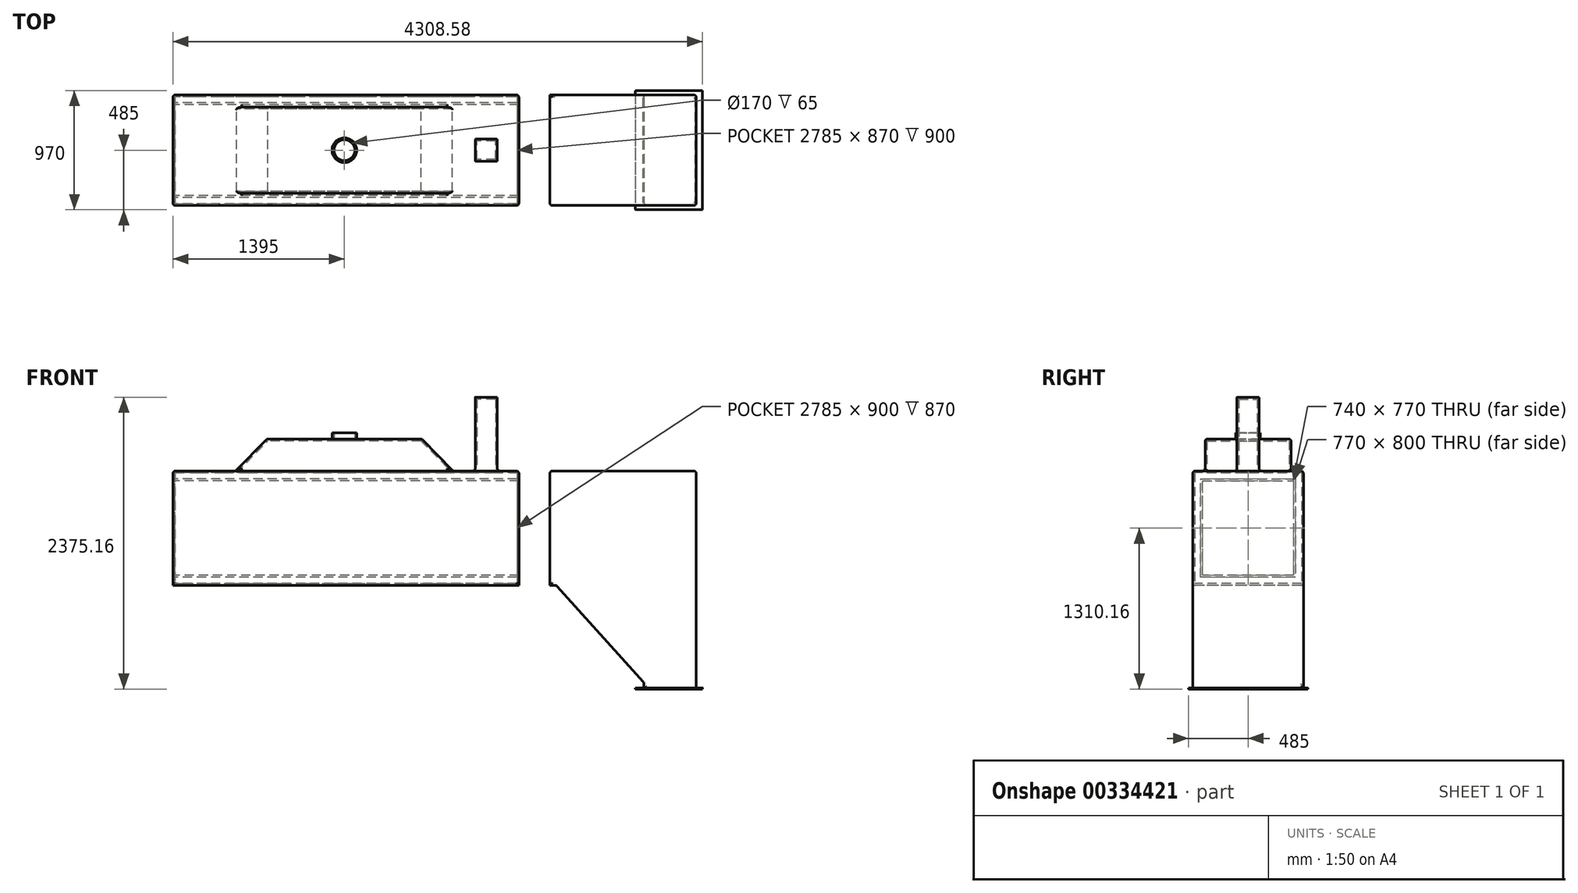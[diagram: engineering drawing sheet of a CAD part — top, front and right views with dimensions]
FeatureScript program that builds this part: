
annotation { "Feature Type Name" : "Feature", "Feature Type Description" : "" }
export const myFeature = defineFeature(function(context is Context, id is Id, definition is map)
    precondition{}
    {
        {
            var Q0;
            Q0=qCreatedBy(makeId("Front.planeOp"),FACE);
            var sketch = newSketch(context, id + "F0", { "sketchPlane" : qUnion([Q0])});
            skLineSegment(sketch, "E0.bottom", {"start": v(1420, 465) * mm, "end": v(-1420, 465) * mm});
            skLineSegment(sketch, "E0.top", {"start": v(1420, -465) * mm, "end": v(-1420, -465) * mm});
            skLineSegment(sketch, "E0.left", {"start": v(1420, 465) * mm, "end": v(1420, -465) * mm});
            skLineSegment(sketch, "E0.right", {"start": v(-1420, 465) * mm, "end": v(-1420, -465) * mm});
            skPoint(sketch, "E0.middle", {"position": v(0, 0) * mm});
            skSolve(sketch);
        }
        {
            var Q0;
            Q0 = qSketchRegion(id + "F0", true);
            extrude(context, id + "F1", {"entities" : qUnion([Q0]), "oppositeDirection" : true, "depth" : 900 * mm});
        }
        {
            var Q0;
            Q0=makeQuery(id+"F1.opExtrude","SWEPT_FACE",FACE,{"disambiguationData":[OSD([sQuery(id+"F0.wireOp",EDGE,"E0.bottom")])]});
            var sketch = newSketch(context, id + "F2", { "sketchPlane" : qUnion([Q0])});
            skLineSegment(sketch, "E1.bottom", {"start": v(885, 100) * mm, "end": v(-885, 100) * mm});
            skLineSegment(sketch, "E1.top", {"start": v(885, 800) * mm, "end": v(-885, 800) * mm});
            skLineSegment(sketch, "E1.left", {"start": v(885, 100) * mm, "end": v(885, 800) * mm});
            skLineSegment(sketch, "E1.right", {"start": v(-885, 100) * mm, "end": v(-885, 800) * mm});
            skPoint(sketch, "E1.middle", {"position": v(0, 450) * mm});
            skLineSegment(sketch, "E2", {"start": v(26.19, 450) * mm, "end": v(-1737.19, 450) * mm, "construction": true});
            skSolve(sketch);
        }
        {
            var Q0;
            Q0=makeQuery(id+"F2.imprint","IMPRINT",FACE,{"disambiguationData":[TD([[makeQuery(id+"F2.imprint","IMPRINT",EDGE,{"derivedFrom":sQuery(id+"F2.wireOp",EDGE,"E1.bottom")}),1.0]])]});
            cPlane(context, id + "F3", {"entities" : qUnion([Q0]), "cplaneType" : CPlaneType.OFFSET, "offset" : 260 * mm, "width" : 150 * mm, "height" : 150 * mm});
        }
        {
            var Q0;
            Q0=qCreatedBy(id+"F3.planeOp",FACE);
            var sketch = newSketch(context, id + "F4", { "sketchPlane" : qUnion([Q0])});
            skLineSegment(sketch, "E3.0", {"start": v(630, 800) * mm, "end": v(-630, 800) * mm});
            skLineSegment(sketch, "E3.1", {"start": v(630, 100) * mm, "end": v(-630, 100) * mm});
            skLineSegment(sketch, "E4", {"start": v(0, 800) * mm, "end": v(0, 100) * mm, "construction": true});
            skLineSegment(sketch, "E5", {"start": v(-630, 800) * mm, "end": v(-630, 100) * mm});
            skLineSegment(sketch, "E6.MirrorCS", {"start": v(630, 800) * mm, "end": v(630, 100) * mm});
            skPoint(sketch, "E7.orphan", {"position": v(-885, 800) * mm});
            skPoint(sketch, "E8.orphan", {"position": v(-885, 100) * mm});
            skPoint(sketch, "E9.orphan", {"position": v(885, 100) * mm});
            skPoint(sketch, "E10.orphan", {"position": v(885, 800) * mm});
            skSolve(sketch);
        }
        {
            var Q1;
            Q1=makeQuery(id+"F2.imprint","IMPRINT",FACE,{"disambiguationData":[TD([[makeQuery(id+"F2.imprint","IMPRINT",EDGE,{"derivedFrom":sQuery(id+"F2.wireOp",EDGE,"E1.bottom")}),-1.0]])]});
            var Q2;
            Q2=makeQuery(id+"F4.imprint","IMPRINT",FACE,{"disambiguationData":[TD([[makeQuery(id+"F4.imprint","IMPRINT",EDGE,{"derivedFrom":sQuery(id+"F4.wireOp",EDGE,"E3.0")}),1.0]])]});
            loft(context, id + "F5", {"operationType" : NewBodyOperationType.ADD, "sheetProfilesArray" : [{ "sheetProfileEntities" : qUnion([Q1]) }, { "sheetProfileEntities" : qUnion([Q2]) }]});
        }
        {
            var Q0;
            Q0=makeQuery(id+"F4.imprint","IMPRINT",FACE,{"disambiguationData":[TD([[makeQuery(id+"F4.imprint","IMPRINT",EDGE,{"derivedFrom":sQuery(id+"F4.wireOp",EDGE,"E3.0")}),1.0]])]});
            var sketch = newSketch(context, id + "F6", { "sketchPlane" : qUnion([Q0])});
            skCircle(sketch, "E11", {"center": v(0, 450) * mm, "radius": 100 * mm});
            skSolve(sketch);
        }
        {
            var Q0;
            Q0 = qSketchRegion(id + "F6", true);
            extrude(context, id + "F7", {"entities" : qUnion([Q0]), "operationType" : NewBodyOperationType.ADD, "depth" : 50 * mm});
        }
        {
            var Q0;
            Q0=makeQuery(id+"F1.opExtrude","SWEPT_FACE",FACE,{"disambiguationData":[OSD([sQuery(id+"F0.wireOp",EDGE,"E0.bottom")])]});
            var sketch = newSketch(context, id + "F8", { "sketchPlane" : qUnion([Q0])});
            skLineSegment(sketch, "E12.bottom", {"start": v(1239.32, 360) * mm, "end": v(1069.32, 360) * mm});
            skLineSegment(sketch, "E12.top", {"start": v(1239.32, 540) * mm, "end": v(1069.32, 540) * mm});
            skLineSegment(sketch, "E12.left", {"start": v(1244.32, 365) * mm, "end": v(1244.32, 535) * mm});
            skLineSegment(sketch, "E12.right", {"start": v(1064.32, 365) * mm, "end": v(1064.32, 535) * mm});
            skPoint(sketch, "E12.middle", {"position": v(1154.32, 450) * mm});
            skPoint(sketch, "E13", {"position": v(885, 450) * mm});
            skPoint(sketch, "E14.visualSharp", {"position": v(1064.32, 360) * mm});
            skArc(sketch, "E14.filletArc", {"start": v(1064.32, 365) * mm, "mid": v(1065.79, 361.46) * mm, "end": v(1069.32, 360) * mm});
            skPoint(sketch, "E15.visualSharp", {"position": v(1244.32, 360) * mm});
            skArc(sketch, "E15.filletArc", {"start": v(1239.32, 360) * mm, "mid": v(1242.86, 361.46) * mm, "end": v(1244.32, 365) * mm});
            skPoint(sketch, "E16.visualSharp", {"position": v(1244.32, 540) * mm});
            skArc(sketch, "E16.filletArc", {"start": v(1244.32, 535) * mm, "mid": v(1242.86, 538.54) * mm, "end": v(1239.32, 540) * mm});
            skPoint(sketch, "E17.visualSharp", {"position": v(1064.32, 540) * mm});
            skArc(sketch, "E17.filletArc", {"start": v(1069.32, 540) * mm, "mid": v(1065.79, 538.54) * mm, "end": v(1064.32, 535) * mm});
            skSolve(sketch);
        }
        {
            var Q0;
            Q0 = qSketchRegion(id + "F8", true);
            extrude(context, id + "F9", {"entities" : qUnion([Q0]), "operationType" : NewBodyOperationType.ADD, "depth" : 600 * mm});
        }
        {
            var Q0;
            Q0=makeQuery(id+"F1.opExtrude","SWEPT_FACE",FACE,{"disambiguationData":[OSD([sQuery(id+"F0.wireOp",EDGE,"E0.right")])]});
            extrude(context, id + "F10", {"entities" : qUnion([Q0]), "operationType" : NewBodyOperationType.REMOVE, "oppositeDirection" : true, "depth" : 25 * mm});
        }
        {
            var Q0;
            Q0=makeQuery(id+"F10.boolean.opBoolean","COPY",FACE,{"derivedFrom":makeQuery(id+"F10.opExtrude","CAP_FACE",FACE,{"disambiguationData":[OSD([sQuery(id+"F0.wireOp",EDGE,"E0.right")])],"isStart":false})});
            var sketch = newSketch(context, id + "F11", { "sketchPlane" : qUnion([Q0])});
            skLineSegment(sketch, "E18.0", {"start": v(-820, 385) * mm, "end": v(-820, -385) * mm});
            skLineSegment(sketch, "E18.1", {"start": v(-30, 385) * mm, "end": v(-820, 385) * mm});
            skLineSegment(sketch, "E19.0", {"start": v(-80, -385) * mm, "end": v(-80, 435) * mm});
            skLineSegment(sketch, "E20.0", {"start": v(-820, -385) * mm, "end": v(-80, -385) * mm});
            skSolve(sketch);
        }
        {
            var Q0;
            Q0 = qSketchRegion(id + "F11", true);
            extrude(context, id + "F12", {"entities" : qUnion([Q0]), "operationType" : NewBodyOperationType.REMOVE, "endBound" : BoundingType.THROUGH_ALL, "oppositeDirection" : true, "depth" : 25 * mm});
        }
        {
            var Q0;
            Q0=makeQuery(id+"F7.opExtrude","CAP_FACE",FACE,{"disambiguationData":[OSD([sQuery(id+"F6.wireOp",EDGE,"E11")])],"isStart":false});
            shell(context, id + "F13", {"entities" : qUnion([Q0]), "thickness" : 15 * mm});
        }
        {
            var Q0;
            Q0=qCreatedBy(makeId("Front.planeOp"),FACE);
            var sketch = newSketch(context, id + "F14", { "sketchPlane" : qUnion([Q0])});
            skLineSegment(sketch, "E21", {"start": v(1672.61, 465) * mm, "end": v(2863.58, 465) * mm});
            skLineSegment(sketch, "E22", {"start": v(2863.58, 465) * mm, "end": v(2863.58, -1310.16) * mm});
            skLineSegment(sketch, "E23", {"start": v(2863.58, -1310.16) * mm, "end": v(2438.58, -1310.16) * mm});
            skLineSegment(sketch, "E24", {"start": v(2438.58, -1310.16) * mm, "end": v(2438.58, -1260.16) * mm});
            skLineSegment(sketch, "E25", {"start": v(2438.58, -1260.16) * mm, "end": v(1722.61, -465) * mm});
            skLineSegment(sketch, "E26", {"start": v(1722.61, -465) * mm, "end": v(1672.61, -465) * mm});
            skLineSegment(sketch, "E27", {"start": v(1672.61, -465) * mm, "end": v(1672.61, 465) * mm});
            skSolve(sketch);
        }
        {
            var Q0;
            Q0 = qSketchRegion(id + "F14", true);
            var Q1;
            Q1=makeQuery(id+"F1.opExtrude","CAP_FACE",FACE,{"disambiguationData":[OSD([sQuery(id+"F0.wireOp",EDGE,"E0.bottom"),sQuery(id+"F0.wireOp",EDGE,"E0.top"),sQuery(id+"F0.wireOp",EDGE,"E0.left"),sQuery(id+"F0.wireOp",EDGE,"E0.right")])],"isStart":false});
            extrude(context, id + "F15", {"entities" : qUnion([Q0]), "endBound" : BoundingType.UP_TO_SURFACE, "oppositeDirection" : true, "endBoundEntityFace" : qUnion([Q1]), "offsetDistance" : 25 * mm, "depth" : 25 * mm});
        }
        {
            var Q0;
            Q0=makeQuery(id+"F15.boolean.opBoolean","MERGE",FACE,{"derivedFrom":[makeQuery(id+"F1.opExtrude","SWEPT_FACE",FACE,{"disambiguationData":[OSD([sQuery(id+"F0.wireOp",EDGE,"E0.bottom")])]}),makeQuery(id+"F15.opExtrude","SWEPT_FACE",FACE,{"disambiguationData":[OSD([sQuery(id+"F14.wireOp",EDGE,"E21")])]})]});
            var Q1;
            Q1=makeQuery(id+"F15.boolean.opBoolean","MERGE",FACE,{"derivedFrom":[makeQuery(id+"F1.opExtrude","CAP_FACE",FACE,{"disambiguationData":[OSD([sQuery(id+"F0.wireOp",EDGE,"E0.bottom"),sQuery(id+"F0.wireOp",EDGE,"E0.top"),sQuery(id+"F0.wireOp",EDGE,"E0.left"),sQuery(id+"F0.wireOp",EDGE,"E0.right")])],"isStart":true}),makeQuery(id+"F15.opExtrude","CAP_FACE",FACE,{"disambiguationData":[OSD([sQuery(id+"F14.wireOp",EDGE,"E21"),sQuery(id+"F14.wireOp",EDGE,"E22"),sQuery(id+"F14.wireOp",EDGE,"E23"),sQuery(id+"F14.wireOp",EDGE,"E24"),sQuery(id+"F14.wireOp",EDGE,"E25"),sQuery(id+"F14.wireOp",EDGE,"E26"),sQuery(id+"F14.wireOp",EDGE,"E27")])],"isStart":true})]});
            var Q2;
            Q2=makeQuery(id+"F15.opExtrude","SWEPT_FACE",FACE,{"disambiguationData":[OSD([sQuery(id+"F14.wireOp",EDGE,"E22")])]});
            var Q3;
            {var subQ0=sQuery(id+"F0.wireOp",EDGE,"E0.right");var subQ1=sQuery(id+"F0.wireOp",EDGE,"E0.left");var subQ2=sQuery(id+"F0.wireOp",EDGE,"E0.top");var subQ3=sQuery(id+"F0.wireOp",EDGE,"E0.bottom");Q3=makeQuery(id+"F15.boolean.opBoolean","MERGE",FACE,{"derivedFrom":[makeQuery(id+"F1.opExtrude","CAP_FACE",FACE,{"disambiguationData":[OSD([subQ3,subQ2,subQ1,subQ0])],"isStart":false}),makeQuery(id+"F15.opExtrude","CAP_FACE",FACE,{"disambiguationData":[OSD([subQ3,subQ2,subQ1,subQ0])],"isStart":false})]});}
            var Q4;
            Q4=makeQuery(id+"F15.opExtrude","SWEPT_FACE",FACE,{"disambiguationData":[OSD([sQuery(id+"F14.wireOp",EDGE,"E25")])]});
            var Q5;
            Q5=makeQuery(id+"F5.opLoft","SWEPT_FACE",FACE,{"disambiguationData":[OSD([sQuery(id+"F2.wireOp",EDGE,"E1.top"),sQuery(id+"F2.wireOp",EDGE,"E1.left"),sQuery(id+"F2.wireOp",EDGE,"E1.right"),sQuery(id+"F4.wireOp",EDGE,"E3.0"),sQuery(id+"F4.wireOp",EDGE,"E5"),sQuery(id+"F4.wireOp",EDGE,"E6.MirrorCS")])]});
            var Q6;
            Q6=makeQuery(id+"F5.opLoft","SWEPT_FACE",FACE,{"disambiguationData":[OSD([sQuery(id+"F2.wireOp",EDGE,"E1.bottom"),sQuery(id+"F2.wireOp",EDGE,"E1.top"),sQuery(id+"F2.wireOp",EDGE,"E1.left"),sQuery(id+"F4.wireOp",EDGE,"E3.0"),sQuery(id+"F4.wireOp",EDGE,"E3.1"),sQuery(id+"F4.wireOp",EDGE,"E6.MirrorCS")])]});
            var Q7;
            Q7=makeQuery(id+"F5.opLoft","SWEPT_FACE",FACE,{"disambiguationData":[OSD([sQuery(id+"F2.wireOp",EDGE,"E1.bottom"),sQuery(id+"F2.wireOp",EDGE,"E1.left"),sQuery(id+"F2.wireOp",EDGE,"E1.right"),sQuery(id+"F4.wireOp",EDGE,"E3.1"),sQuery(id+"F4.wireOp",EDGE,"E5"),sQuery(id+"F4.wireOp",EDGE,"E6.MirrorCS")])]});
            var Q8;
            Q8=makeQuery(id+"F5.opLoft","SWEPT_FACE",FACE,{"disambiguationData":[OSD([sQuery(id+"F2.wireOp",EDGE,"E1.bottom"),sQuery(id+"F2.wireOp",EDGE,"E1.top"),sQuery(id+"F2.wireOp",EDGE,"E1.right"),sQuery(id+"F4.wireOp",EDGE,"E3.0"),sQuery(id+"F4.wireOp",EDGE,"E3.1"),sQuery(id+"F4.wireOp",EDGE,"E5")])]});
            var Q9;
            Q9=makeQuery(id+"F7.opExtrude","CAP_EDGE",EDGE,{"disambiguationData":[OSD([sQuery(id+"F6.wireOp",EDGE,"E11")])],"isStart":true});
            fillet(context, id + "F16", {"entities" : qUnion([Q0, Q1, Q2, Q3, Q4, Q5, Q6, Q7, Q8, Q9]), "radius" : 20 * mm, "tangentPropagation" : true, "allowEdgeOverflow" : false});
        }
        {
            var Q0;
            Q0=makeQuery(id+"F15.opExtrude","SWEPT_FACE",FACE,{"disambiguationData":[OSD([sQuery(id+"F14.wireOp",EDGE,"E23")])]});
            var sketch = newSketch(context, id + "F17", { "sketchPlane" : qUnion([Q0])});
            skLineSegment(sketch, "E28", {"start": v(2438.58, -450) * mm, "end": v(2843.58, -450) * mm, "construction": true});
            skLineSegment(sketch, "E29", {"start": v(2641.08, -20) * mm, "end": v(2641.08, -880) * mm, "construction": true});
            skLineSegment(sketch, "E30.bottom", {"start": v(2908.58, -935) * mm, "end": v(2373.58, -935) * mm});
            skLineSegment(sketch, "E30.top", {"start": v(2908.58, 35) * mm, "end": v(2373.58, 35) * mm});
            skLineSegment(sketch, "E30.left", {"start": v(2913.58, -930) * mm, "end": v(2913.58, 30) * mm});
            skLineSegment(sketch, "E30.right", {"start": v(2368.58, -930) * mm, "end": v(2368.58, 30) * mm});
            skPoint(sketch, "E30.middle", {"position": v(2641.08, -450) * mm});
            skLineSegment(sketch, "E31.bottom", {"start": v(2853.58, -875) * mm, "end": v(2428.58, -875) * mm});
            skLineSegment(sketch, "E31.top", {"start": v(2853.58, -25) * mm, "end": v(2428.58, -25) * mm});
            skLineSegment(sketch, "E31.left", {"start": v(2853.58, -875) * mm, "end": v(2853.58, -25) * mm});
            skLineSegment(sketch, "E31.right", {"start": v(2428.58, -875) * mm, "end": v(2428.58, -25) * mm});
            skPoint(sketch, "E32.visualSharp", {"position": v(2368.58, 35) * mm});
            skArc(sketch, "E32.filletArc", {"start": v(2373.58, 35) * mm, "mid": v(2370.04, 33.54) * mm, "end": v(2368.58, 30) * mm});
            skPoint(sketch, "E33.visualSharp", {"position": v(2913.58, 35) * mm});
            skArc(sketch, "E33.filletArc", {"start": v(2913.58, 30) * mm, "mid": v(2912.12, 33.54) * mm, "end": v(2908.58, 35) * mm});
            skPoint(sketch, "E34.visualSharp", {"position": v(2913.58, -935) * mm});
            skArc(sketch, "E34.filletArc", {"start": v(2908.58, -935) * mm, "mid": v(2912.12, -933.54) * mm, "end": v(2913.58, -930) * mm});
            skPoint(sketch, "E35.visualSharp", {"position": v(2368.58, -935) * mm});
            skArc(sketch, "E35.filletArc", {"start": v(2368.58, -930) * mm, "mid": v(2370.04, -933.54) * mm, "end": v(2373.58, -935) * mm});
            skSolve(sketch);
        }
        {
            var Q0;
            Q0 = qSketchRegion(id + "F17", true);
            extrude(context, id + "F18", {"entities" : qUnion([Q0]), "operationType" : NewBodyOperationType.ADD, "oppositeDirection" : true, "depth" : 10 * mm});
        }
    });
